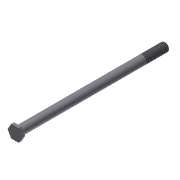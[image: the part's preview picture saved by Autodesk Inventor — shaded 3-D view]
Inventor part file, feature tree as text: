
AUTODESK INVENTOR PART (.ipt)
format: ipt  version: 2013 (Build 170138000, 138)  size: 88,576 bytes
history: native  units: in
note: dims shown in document units (in); Inventor stores cm internally (conversion verified against a paired STEP export)
features: extrude x2, sketch x2, thread x1, chamfer x1
ambient origin geometry x8: Origin, YZ Plane, XZ Plane, XY Plane, X Axis, Y Axis, Z Axis, Center Point
bodies: Solid1 (feature_tree)
feature tree (6):
  extrude  "Extrusion1"  Depth=6.5in TaperAngle=0.0deg
  extrude  "Extrusion2"  Depth=0.125in TaperAngle=0.0deg
  thread  "Thread1"  [1 undecoded]
  chamfer  "Chamfer1"  Distance=0.02in Angle=45.0deg
  sketch  "Sketch1"  dims[d0=0.375in d1=6.5in d2=0.0in]
  sketch  "Sketch2"  dims[d3=0.5625in d4=0.125in d5=0.0in d6=1.0in d7=0.0in d8=0.02in d9=0.125in d10=45.0deg]
note: 1 required parameter value undecoded (feature->parameter linkage not recoverable at this tier; creation-order binding heuristic only, values carry confidence <= 0.55)
